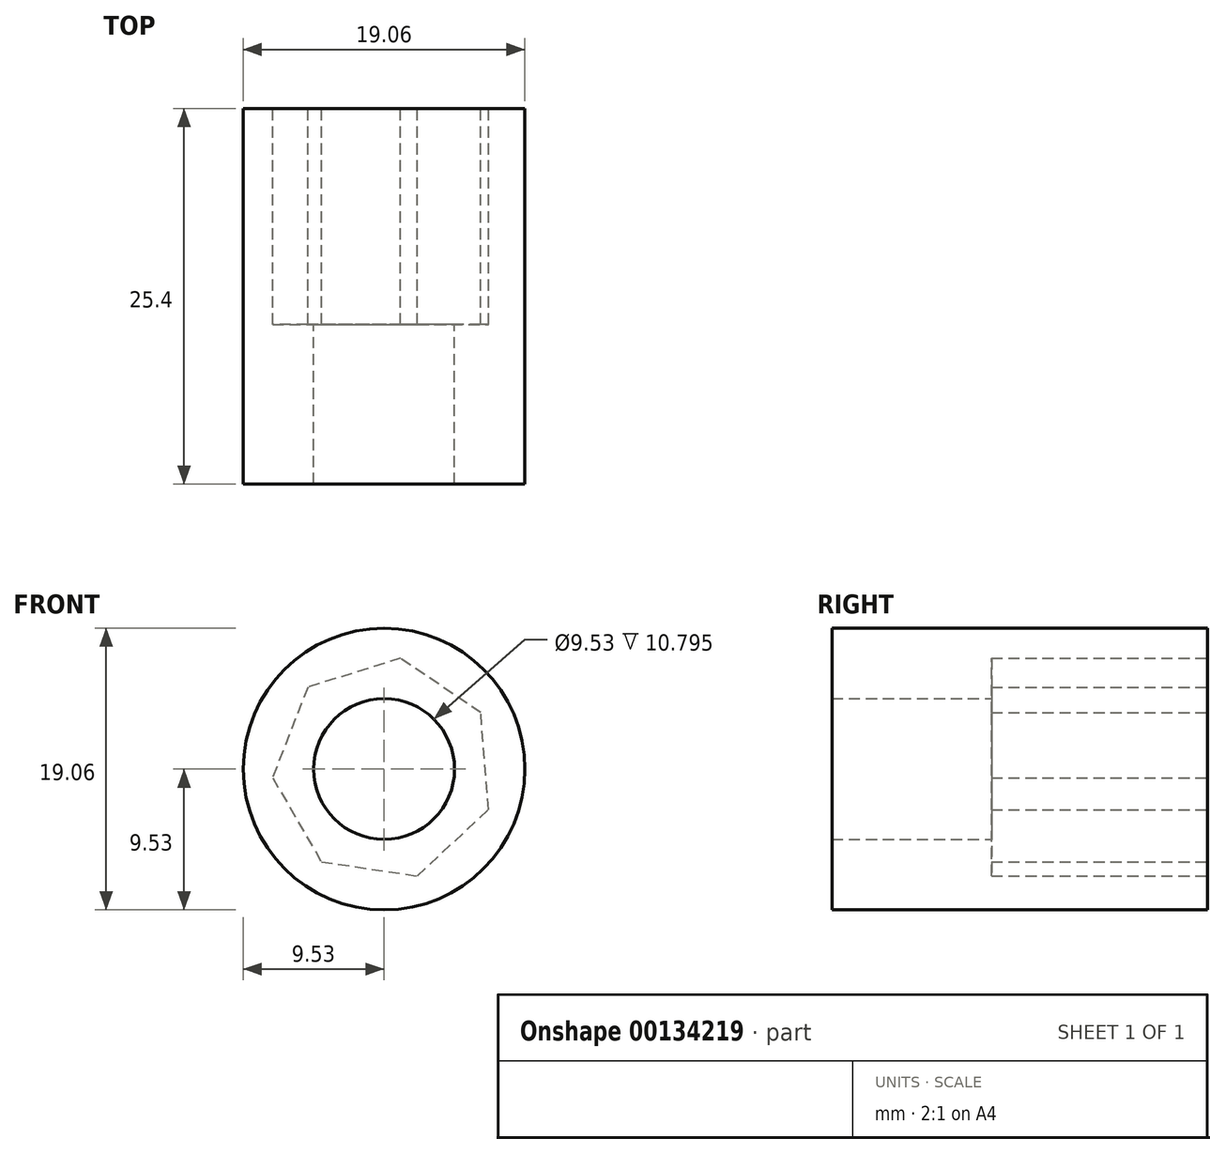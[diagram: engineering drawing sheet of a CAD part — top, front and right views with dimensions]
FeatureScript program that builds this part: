
annotation { "Feature Type Name" : "Feature", "Feature Type Description" : "" }
export const myFeature = defineFeature(function(context is Context, id is Id, definition is map)
    precondition{}
    {
        {
            var Q0;
            Q0=qCreatedBy(makeId("Front.planeOp"),FACE);
            var sketch = newSketch(context, id + "F0", { "sketchPlane" : qUnion([Q0])});
            skCircle(sketch, "E0", {"center": v(0, 0) * mm, "radius": 9.53 * mm});
            skSolve(sketch);
        }
        {
            var Q0;
            Q0 = qSketchRegion(id + "F0", true);
            extrude(context, id + "F1", {"entities" : qUnion([Q0]), "depth" : 25.4 * mm});
        }
        {
            var Q0;
            Q0=qCreatedBy(makeId("Front.planeOp"),FACE);
            var sketch = newSketch(context, id + "F2", { "sketchPlane" : qUnion([Q0])});
            skLineSegment(sketch, "E1.bottom", {"start": v(4.76, 4.76) * mm, "end": v(-4.76, 4.76) * mm});
            skLineSegment(sketch, "E1.top", {"start": v(4.76, -4.76) * mm, "end": v(-4.76, -4.76) * mm});
            skLineSegment(sketch, "E1.left", {"start": v(4.76, 4.76) * mm, "end": v(4.76, -4.76) * mm});
            skLineSegment(sketch, "E1.right", {"start": v(-4.76, 4.76) * mm, "end": v(-4.76, -4.76) * mm});
            skPoint(sketch, "E1.middle", {"position": v(0, 0) * mm});
            skSolve(sketch);
        }
        {
            var Q0;
            Q0=qCreatedBy(makeId("Front.planeOp"),FACE);
            var sketch = newSketch(context, id + "F3", { "sketchPlane" : qUnion([Q0])});
            skCircle(sketch, "E2", {"center": v(0, 0) * mm, "radius": 4.76 * mm});
            skSolve(sketch);
        }
        {
            var Q0;
            Q0 = qSketchRegion(id + "F3", true);
            extrude(context, id + "F4", {"entities" : qUnion([Q0]), "operationType" : NewBodyOperationType.REMOVE, "endBound" : BoundingType.THROUGH_ALL, "depth" : 25.4 * mm});
        }
        {
            var Q0;
            Q0 = qSketchRegion(id + "F2", true);
            extrude(context, id + "F5", {"entities" : qUnion([Q0]), "operationType" : NewBodyOperationType.REMOVE, "depth" : 11.1 * mm});
        }
        {
            var Q0;
            Q0=makeQuery(id+"F1.opExtrude","CAP_FACE",FACE,{"disambiguationData":[OSD([sQuery(id+"F0.wireOp",EDGE,"E0")])],"isStart":true});
            var sketch = newSketch(context, id + "F6", { "sketchPlane" : qUnion([Q0])});
            skCircle(sketch, "E3.cCircle", {"center": v(0, 0) * mm, "radius": 6.82 * mm, "construction": true});
            skLineSegment(sketch, "E3.0", {"start": v(7.55, -0.59) * mm, "end": v(4.25, -6.27) * mm});
            skLineSegment(sketch, "E3.1", {"start": v(4.25, -6.27) * mm, "end": v(-2.25, -7.23) * mm});
            skLineSegment(sketch, "E3.2", {"start": v(-2.25, -7.23) * mm, "end": v(-7.06, -2.75) * mm});
            skLineSegment(sketch, "E3.3", {"start": v(-7.06, -2.75) * mm, "end": v(-6.55, 3.8) * mm});
            skLineSegment(sketch, "E3.4", {"start": v(-6.55, 3.8) * mm, "end": v(-1.1, 7.5) * mm});
            skLineSegment(sketch, "E3.5", {"start": v(-1.1, 7.5) * mm, "end": v(5.17, 5.54) * mm});
            skLineSegment(sketch, "E3.6", {"start": v(5.17, 5.54) * mm, "end": v(7.55, -0.59) * mm});
            skPoint(sketch, "E3.0.midPoint", {"position": v(5.9, -3.43) * mm});
            skSolve(sketch);
        }
        {
            var Q0;
            Q0 = qSketchRegion(id + "F6", true);
            extrude(context, id + "F7", {"entities" : qUnion([Q0]), "operationType" : NewBodyOperationType.REMOVE, "oppositeDirection" : true, "depth" : 14.6 * mm});
        }
    });
